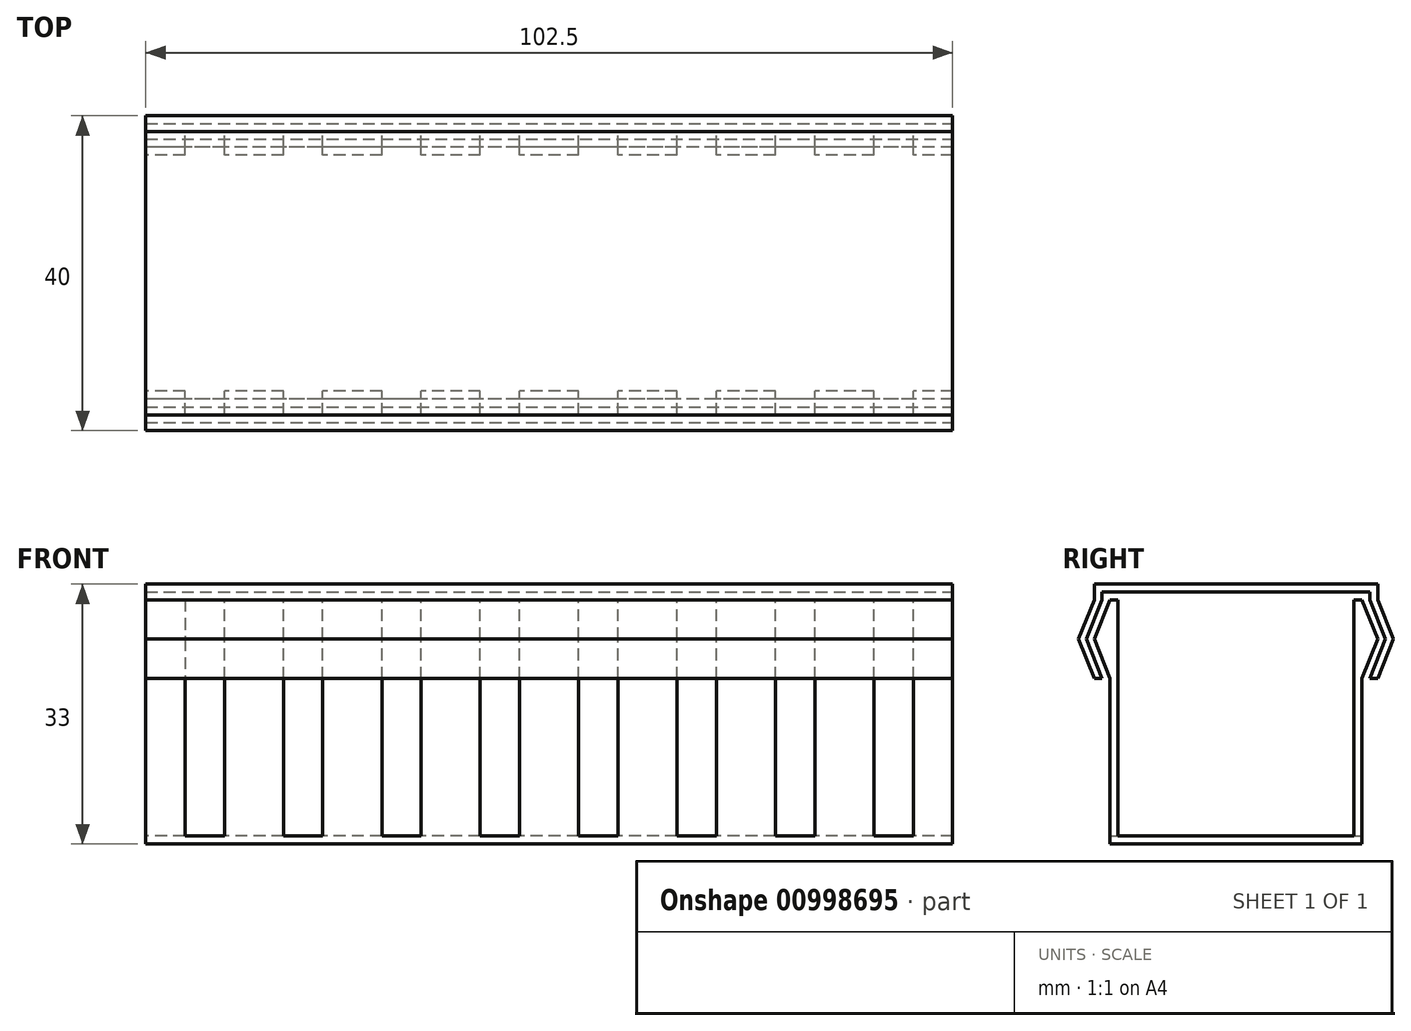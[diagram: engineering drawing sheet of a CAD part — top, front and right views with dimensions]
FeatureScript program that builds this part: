
annotation { "Feature Type Name" : "Feature", "Feature Type Description" : "" }
export const myFeature = defineFeature(function(context is Context, id is Id, definition is map)
    precondition{}
    {
        {
            var Q0;
            Q0=qCreatedBy(makeId("Right.planeOp"),FACE);
            var sketch = newSketch(context, id + "F0", { "sketchPlane" : qUnion([Q0])});
            skLineSegment(sketch, "E0", {"start": v(-32, 31) * mm, "end": v(-32, 0) * mm});
            skLineSegment(sketch, "E1", {"start": v(-32, 0) * mm, "end": v(0, 0) * mm});
            skLineSegment(sketch, "E2", {"start": v(0, 0) * mm, "end": v(0, 0) * mm});
            skLineSegment(sketch, "E3", {"start": v(0, 0) * mm, "end": v(0, 31) * mm});
            skLineSegment(sketch, "E4", {"start": v(0, 31) * mm, "end": v(-1, 31) * mm});
            skLineSegment(sketch, "E5", {"start": v(-1, 31) * mm, "end": v(-1, 1) * mm});
            skLineSegment(sketch, "E6", {"start": v(-1, 1) * mm, "end": v(-31, 1) * mm});
            skLineSegment(sketch, "E7", {"start": v(-31, 1) * mm, "end": v(-31, 31) * mm});
            skLineSegment(sketch, "E8", {"start": v(-31, 31) * mm, "end": v(-32, 31) * mm});
            skLineSegment(sketch, "E9", {"start": v(-16, 0) * mm, "end": v(-16, 1) * mm, "construction": true});
            skLineSegment(sketch, "E10", {"start": v(-32, 31) * mm, "end": v(-34, 26) * mm});
            skLineSegment(sketch, "E11", {"start": v(-34, 26) * mm, "end": v(-32, 26) * mm});
            skLineSegment(sketch, "E12", {"start": v(0, 31) * mm, "end": v(2, 26) * mm});
            skLineSegment(sketch, "E13", {"start": v(2, 26) * mm, "end": v(0, 26) * mm});
            skLineSegment(sketch, "E14", {"start": v(-34, 26) * mm, "end": v(-32, 21) * mm});
            skLineSegment(sketch, "E15", {"start": v(2, 26) * mm, "end": v(0, 21) * mm});
            skSolve(sketch);
        }
        {
            var Q0;
            Q0 = qSketchRegion(id + "F0", true);
            extrude(context, id + "F1", {"entities" : qUnion([Q0]), "depth" : 102.5 * mm, "offsetDistance" : 25 * mm});
        }
        {
            var Q0;
            Q0=makeQuery(id+"F1.opExtrude","SWEPT_FACE",FACE,{"disambiguationData":[OSD([sQuery(id+"F0.wireOp",EDGE,"E3")])]});
            var sketch = newSketch(context, id + "F2", { "sketchPlane" : qUnion([Q0])});
            skLineSegment(sketch, "E16.bottom", {"start": v(-97.5, 31) * mm, "end": v(-92.5, 31) * mm});
            skLineSegment(sketch, "E16.top", {"start": v(-97.5, 1) * mm, "end": v(-92.5, 1) * mm});
            skLineSegment(sketch, "E16.left", {"start": v(-97.5, 31) * mm, "end": v(-97.5, 1) * mm});
            skLineSegment(sketch, "E16.right", {"start": v(-92.5, 31) * mm, "end": v(-92.5, 1) * mm});
            skLineSegment(sketch, "E17.1.0.0", {"start": v(-85, 31) * mm, "end": v(-80, 31) * mm});
            skLineSegment(sketch, "E17.1.0.1", {"start": v(-80, 31) * mm, "end": v(-80, 1) * mm});
            skLineSegment(sketch, "E17.1.0.2", {"start": v(-85, 31) * mm, "end": v(-85, 1) * mm});
            skLineSegment(sketch, "E17.1.0.3", {"start": v(-85, 1) * mm, "end": v(-80, 1) * mm});
            skLineSegment(sketch, "E17.2.0.0", {"start": v(-72.5, 31) * mm, "end": v(-67.5, 31) * mm});
            skLineSegment(sketch, "E17.2.0.1", {"start": v(-67.5, 31) * mm, "end": v(-67.5, 1) * mm});
            skLineSegment(sketch, "E17.2.0.2", {"start": v(-72.5, 31) * mm, "end": v(-72.5, 1) * mm});
            skLineSegment(sketch, "E17.2.0.3", {"start": v(-72.5, 1) * mm, "end": v(-67.5, 1) * mm});
            skLineSegment(sketch, "E17.3.0.0", {"start": v(-60, 31) * mm, "end": v(-55, 31) * mm});
            skLineSegment(sketch, "E17.3.0.1", {"start": v(-55, 31) * mm, "end": v(-55, 1) * mm});
            skLineSegment(sketch, "E17.3.0.2", {"start": v(-60, 31) * mm, "end": v(-60, 1) * mm});
            skLineSegment(sketch, "E17.3.0.3", {"start": v(-60, 1) * mm, "end": v(-55, 1) * mm});
            skLineSegment(sketch, "E17.4.0.0", {"start": v(-47.5, 31) * mm, "end": v(-42.5, 31) * mm});
            skLineSegment(sketch, "E17.4.0.1", {"start": v(-42.5, 31) * mm, "end": v(-42.5, 1) * mm});
            skLineSegment(sketch, "E17.4.0.2", {"start": v(-47.5, 31) * mm, "end": v(-47.5, 1) * mm});
            skLineSegment(sketch, "E17.4.0.3", {"start": v(-47.5, 1) * mm, "end": v(-42.5, 1) * mm});
            skLineSegment(sketch, "E17.5.0.0", {"start": v(-35, 31) * mm, "end": v(-30, 31) * mm});
            skLineSegment(sketch, "E17.5.0.1", {"start": v(-30, 31) * mm, "end": v(-30, 1) * mm});
            skLineSegment(sketch, "E17.5.0.2", {"start": v(-35, 31) * mm, "end": v(-35, 1) * mm});
            skLineSegment(sketch, "E17.5.0.3", {"start": v(-35, 1) * mm, "end": v(-30, 1) * mm});
            skLineSegment(sketch, "E17.6.0.0", {"start": v(-22.5, 31) * mm, "end": v(-17.5, 31) * mm});
            skLineSegment(sketch, "E17.6.0.1", {"start": v(-17.5, 31) * mm, "end": v(-17.5, 1) * mm});
            skLineSegment(sketch, "E17.6.0.2", {"start": v(-22.5, 31) * mm, "end": v(-22.5, 1) * mm});
            skLineSegment(sketch, "E17.6.0.3", {"start": v(-22.5, 1) * mm, "end": v(-17.5, 1) * mm});
            skLineSegment(sketch, "E17.7.0.0", {"start": v(-10, 31) * mm, "end": v(-5, 31) * mm});
            skLineSegment(sketch, "E17.7.0.1", {"start": v(-5, 31) * mm, "end": v(-5, 1) * mm});
            skLineSegment(sketch, "E17.7.0.2", {"start": v(-10, 31) * mm, "end": v(-10, 1) * mm});
            skLineSegment(sketch, "E17.7.0.3", {"start": v(-10, 1) * mm, "end": v(-5, 1) * mm});
            skLineSegment(sketch, "E17.direction1", {"start": v(-97.5, 1) * mm, "end": v(-85, 1) * mm, "construction": true});
            skSolve(sketch);
        }
        {
            var Q0;
            Q0 = qSketchRegion(id + "F2", true);
            extrude(context, id + "F3", {"entities" : qUnion([Q0]), "operationType" : NewBodyOperationType.REMOVE, "endBound" : BoundingType.THROUGH_ALL, "oppositeDirection" : true, "depth" : 25 * mm, "offsetDistance" : 25 * mm});
        }
        {
            var Q0;
            Q0 = qSketchRegion(id + "F2", true);
            extrude(context, id + "F4", {"entities" : qUnion([Q0]), "operationType" : NewBodyOperationType.REMOVE, "endBound" : BoundingType.THROUGH_ALL, "depth" : 34.1 * mm, "offsetDistance" : 25 * mm});
        }
        {
            var Q0;
            Q0=makeQuery(id+"F1.opExtrude","CAP_FACE",FACE,{"disambiguationData":[OSD([sQuery(id+"F0.wireOp",EDGE,"E0"),sQuery(id+"F0.wireOp",EDGE,"E1"),sQuery(id+"F0.wireOp",EDGE,"E3"),sQuery(id+"F0.wireOp",EDGE,"E4"),sQuery(id+"F0.wireOp",EDGE,"E5"),sQuery(id+"F0.wireOp",EDGE,"E6"),sQuery(id+"F0.wireOp",EDGE,"E7"),sQuery(id+"F0.wireOp",EDGE,"E8"),sQuery(id+"F0.wireOp",EDGE,"E10"),sQuery(id+"F0.wireOp",EDGE,"E12"),sQuery(id+"F0.wireOp",EDGE,"E14"),sQuery(id+"F0.wireOp",EDGE,"E15")])],"isStart":false});
            var sketch = newSketch(context, id + "F5", { "sketchPlane" : qUnion([Q0])});
            skLineSegment(sketch, "E18", {"start": v(-34, 26) * mm, "end": v(-35, 26) * mm, "construction": true});
            skLineSegment(sketch, "E19", {"start": v(-32, 21) * mm, "end": v(-33, 21) * mm, "construction": true});
            skLineSegment(sketch, "E20", {"start": v(-32, 31) * mm, "end": v(-33, 31) * mm, "construction": true});
            skLineSegment(sketch, "E21", {"start": v(0, 31) * mm, "end": v(1, 31) * mm, "construction": true});
            skLineSegment(sketch, "E22", {"start": v(2, 26) * mm, "end": v(3, 26) * mm, "construction": true});
            skLineSegment(sketch, "E23", {"start": v(0, 21) * mm, "end": v(1, 21) * mm, "construction": true});
            skLineSegment(sketch, "E24", {"start": v(-33, 21) * mm, "end": v(-34, 21) * mm});
            skLineSegment(sketch, "E25", {"start": v(-33, 21) * mm, "end": v(-35, 26) * mm});
            skLineSegment(sketch, "E26", {"start": v(-35, 26) * mm, "end": v(-33, 31) * mm});
            skLineSegment(sketch, "E27", {"start": v(1, 21) * mm, "end": v(3, 26) * mm});
            skLineSegment(sketch, "E28", {"start": v(1, 31) * mm, "end": v(3, 26) * mm});
            skLineSegment(sketch, "E29", {"start": v(1, 21) * mm, "end": v(2, 21) * mm});
            skLineSegment(sketch, "E30", {"start": v(3, 26) * mm, "end": v(4, 26) * mm, "construction": true});
            skLineSegment(sketch, "E31", {"start": v(1, 31) * mm, "end": v(2, 31) * mm, "construction": true});
            skLineSegment(sketch, "E32", {"start": v(2, 31) * mm, "end": v(2, 32) * mm, "construction": true});
            skLineSegment(sketch, "E33", {"start": v(-35, 26) * mm, "end": v(-36, 26) * mm, "construction": true});
            skLineSegment(sketch, "E34", {"start": v(-34, 21) * mm, "end": v(-36, 26) * mm});
            skLineSegment(sketch, "E35", {"start": v(-33, 31) * mm, "end": v(-34, 31) * mm, "construction": true});
            skLineSegment(sketch, "E36", {"start": v(-34, 31) * mm, "end": v(-34, 32) * mm, "construction": true});
            skLineSegment(sketch, "E37", {"start": v(-36, 26) * mm, "end": v(-34, 31) * mm});
            skLineSegment(sketch, "E38", {"start": v(2, 21) * mm, "end": v(4, 26) * mm});
            skLineSegment(sketch, "E39", {"start": v(4, 26) * mm, "end": v(2, 31) * mm});
            skLineSegment(sketch, "E40", {"start": v(2, 31) * mm, "end": v(2, 32) * mm});
            skLineSegment(sketch, "E41", {"start": v(2, 32) * mm, "end": v(-34, 32) * mm});
            skLineSegment(sketch, "E42", {"start": v(-33, 31) * mm, "end": v(-33, 32) * mm});
            skLineSegment(sketch, "E43", {"start": v(-34, 31) * mm, "end": v(-34, 32) * mm});
            skLineSegment(sketch, "E44", {"start": v(1, 31) * mm, "end": v(1, 32) * mm});
            skLineSegment(sketch, "E45", {"start": v(2, 32) * mm, "end": v(2, 33) * mm});
            skLineSegment(sketch, "E46", {"start": v(2, 33) * mm, "end": v(-34, 33) * mm});
            skLineSegment(sketch, "E47", {"start": v(-34, 33) * mm, "end": v(-34, 32) * mm});
            skSolve(sketch);
        }
        {
            var Q0;
            Q0 = qSketchRegion(id + "F5", true);
            var Q1;
            Q1=makeQuery(id+"F1.opExtrude","CAP_FACE",FACE,{"disambiguationData":[OSD([sQuery(id+"F0.wireOp",EDGE,"E0"),sQuery(id+"F0.wireOp",EDGE,"E1"),sQuery(id+"F0.wireOp",EDGE,"E3"),sQuery(id+"F0.wireOp",EDGE,"E4"),sQuery(id+"F0.wireOp",EDGE,"E5"),sQuery(id+"F0.wireOp",EDGE,"E6"),sQuery(id+"F0.wireOp",EDGE,"E7"),sQuery(id+"F0.wireOp",EDGE,"E8"),sQuery(id+"F0.wireOp",EDGE,"E10"),sQuery(id+"F0.wireOp",EDGE,"E12"),sQuery(id+"F0.wireOp",EDGE,"E14"),sQuery(id+"F0.wireOp",EDGE,"E15")])],"isStart":true});
            extrude(context, id + "F6", {"entities" : qUnion([Q0]), "endBound" : BoundingType.UP_TO_SURFACE, "oppositeDirection" : true, "depth" : 25 * mm, "endBoundEntityFace" : qUnion([Q1]), "offsetDistance" : 25 * mm});
        }
    });
